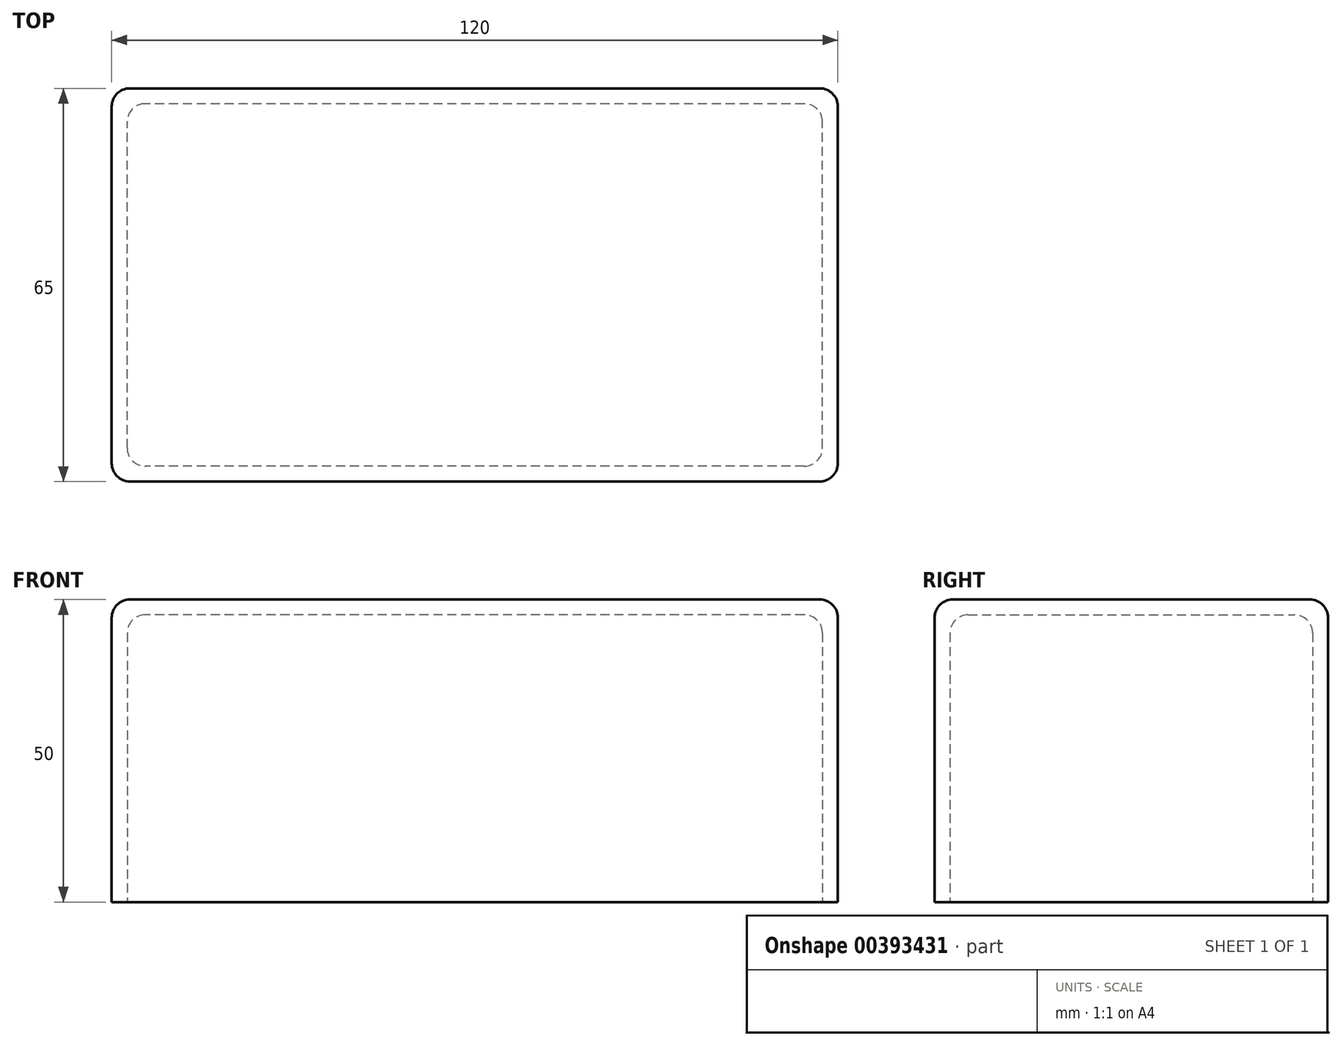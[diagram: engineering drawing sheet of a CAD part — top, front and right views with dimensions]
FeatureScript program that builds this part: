
annotation { "Feature Type Name" : "Feature", "Feature Type Description" : "" }
export const myFeature = defineFeature(function(context is Context, id is Id, definition is map)
    precondition{}
    {
        {
            var Q0;
            Q0=qCreatedBy(makeId("Top.planeOp"),FACE);
            var sketch = newSketch(context, id + "F0", { "sketchPlane" : qUnion([Q0])});
            skLineSegment(sketch, "E0.bottom", {"start": v(60, -32.5) * mm, "end": v(-60, -32.5) * mm});
            skLineSegment(sketch, "E0.top", {"start": v(60, 32.5) * mm, "end": v(-60, 32.5) * mm});
            skLineSegment(sketch, "E0.left", {"start": v(60, -32.5) * mm, "end": v(60, 32.5) * mm});
            skLineSegment(sketch, "E0.right", {"start": v(-60, -32.5) * mm, "end": v(-60, 32.5) * mm});
            skPoint(sketch, "E0.middle", {"position": v(0, 0) * mm});
            skSolve(sketch);
        }
        {
            var Q0;
            Q0=makeQuery(id+"F0.imprint","IMPRINT",FACE,{"disambiguationData":[TD([[makeQuery(id+"F0.imprint","IMPRINT",EDGE,{"derivedFrom":sQuery(id+"F0.wireOp",EDGE,"E0.bottom")}),-1.0]])]});
            extrude(context, id + "F1", {"entities" : qUnion([Q0]), "depth" : 50 * mm});
        }
        {
            var Q0;
            Q0=makeQuery(id+"F1.opExtrude","CAP_FACE",FACE,{"disambiguationData":[OSD([sQuery(id+"F0.wireOp",EDGE,"E0.bottom"),sQuery(id+"F0.wireOp",EDGE,"E0.top"),sQuery(id+"F0.wireOp",EDGE,"E0.left"),sQuery(id+"F0.wireOp",EDGE,"E0.right")])],"isStart":true});
            shell(context, id + "F2", {"entities" : qUnion([Q0]), "thickness" : 2.54 * mm});
        }
        {
            var Q0;
            Q0=makeQuery(id+"F1.opExtrude","CAP_FACE",FACE,{"disambiguationData":[OSD([sQuery(id+"F0.wireOp",EDGE,"E0.bottom"),sQuery(id+"F0.wireOp",EDGE,"E0.top"),sQuery(id+"F0.wireOp",EDGE,"E0.left"),sQuery(id+"F0.wireOp",EDGE,"E0.right")])],"isStart":false});
            var Q1;
            Q1=makeQuery(id+"F1.opExtrude","SWEPT_EDGE",EDGE,{"disambiguationData":[OSD([sQuery(id+"F0.wireOp",EDGE,"E0.top"),sQuery(id+"F0.wireOp",EDGE,"E0.right")])]});
            var Q2;
            Q2=makeQuery(id+"F1.opExtrude","SWEPT_EDGE",EDGE,{"disambiguationData":[OSD([sQuery(id+"F0.wireOp",EDGE,"E0.top"),sQuery(id+"F0.wireOp",EDGE,"E0.left")])]});
            var Q3;
            Q3=makeQuery(id+"F1.opExtrude","SWEPT_EDGE",EDGE,{"disambiguationData":[OSD([sQuery(id+"F0.wireOp",EDGE,"E0.bottom"),sQuery(id+"F0.wireOp",EDGE,"E0.left")])]});
            var Q4;
            Q4=makeQuery(id+"F1.opExtrude","SWEPT_EDGE",EDGE,{"disambiguationData":[OSD([sQuery(id+"F0.wireOp",EDGE,"E0.bottom"),sQuery(id+"F0.wireOp",EDGE,"E0.right")])]});
            fillet(context, id + "F3", {"entities" : qUnion([Q0, Q1, Q2, Q3, Q4]), "radius" : 3 * mm, "tangentPropagation" : true, "allowEdgeOverflow" : false});
        }
        {
            var Q0;
            {var subQ0=sQuery(id+"F0.wireOp",EDGE,"E0.top");Q0=makeQuery(id+"F2.opShell","OFFSET_EDGE",EDGE,{"disambiguationData":[OSD([subQ0]),TDD([makeQuery(id+"F1.opExtrude","CAP_EDGE",EDGE,{"disambiguationData":[OSD([subQ0])],"isStart":false})])]});}
            var Q1;
            {var subQ0=sQuery(id+"F0.wireOp",EDGE,"E0.right");Q1=makeQuery(id+"F2.opShell","OFFSET_EDGE",EDGE,{"disambiguationData":[OSD([subQ0]),TDD([makeQuery(id+"F1.opExtrude","CAP_EDGE",EDGE,{"disambiguationData":[OSD([subQ0])],"isStart":false})])]});}
            var Q2;
            {var subQ0=sQuery(id+"F0.wireOp",EDGE,"E0.bottom");Q2=makeQuery(id+"F2.opShell","OFFSET_EDGE",EDGE,{"disambiguationData":[OSD([subQ0]),TDD([makeQuery(id+"F1.opExtrude","CAP_EDGE",EDGE,{"disambiguationData":[OSD([subQ0])],"isStart":false})])]});}
            var Q3;
            {var subQ0=sQuery(id+"F0.wireOp",EDGE,"E0.left");Q3=makeQuery(id+"F2.opShell","OFFSET_EDGE",EDGE,{"disambiguationData":[OSD([subQ0]),TDD([makeQuery(id+"F1.opExtrude","CAP_EDGE",EDGE,{"disambiguationData":[OSD([subQ0])],"isStart":false})])]});}
            var Q4;
            Q4=makeQuery(id+"F2.opShell","OFFSET_EDGE",EDGE,{"disambiguationData":[OSD([sQuery(id+"F0.wireOp",EDGE,"E0.bottom"),sQuery(id+"F0.wireOp",EDGE,"E0.left")])]});
            var Q5;
            Q5=makeQuery(id+"F2.opShell","OFFSET_EDGE",EDGE,{"disambiguationData":[OSD([sQuery(id+"F0.wireOp",EDGE,"E0.top"),sQuery(id+"F0.wireOp",EDGE,"E0.left")])]});
            var Q6;
            Q6=makeQuery(id+"F2.opShell","OFFSET_EDGE",EDGE,{"disambiguationData":[OSD([sQuery(id+"F0.wireOp",EDGE,"E0.top"),sQuery(id+"F0.wireOp",EDGE,"E0.right")])]});
            var Q7;
            Q7=makeQuery(id+"F2.opShell","OFFSET_EDGE",EDGE,{"disambiguationData":[OSD([sQuery(id+"F0.wireOp",EDGE,"E0.bottom"),sQuery(id+"F0.wireOp",EDGE,"E0.right")])]});
            fillet(context, id + "F4", {"entities" : qUnion([Q0, Q1, Q2, Q3, Q4, Q5, Q6, Q7]), "radius" : 3 * mm, "tangentPropagation" : true, "allowEdgeOverflow" : false});
        }
    });
